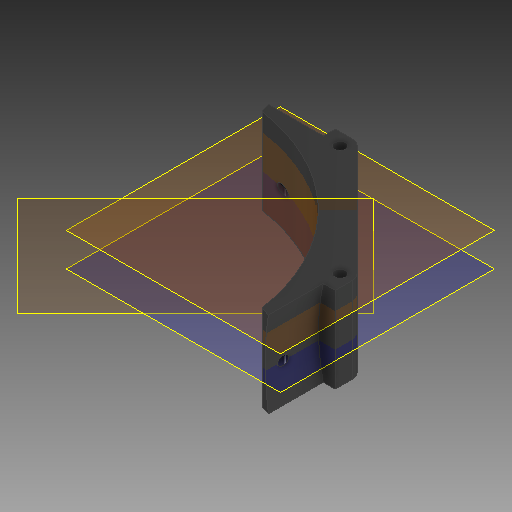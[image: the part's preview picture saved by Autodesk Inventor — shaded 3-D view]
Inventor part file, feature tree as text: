
AUTODESK INVENTOR PART (.ipt)
format: ipt  version: 2020 (Build 240168000, 168)  size: 210,944 bytes
history: native  units: mm
features: sketch x8, extrude x7, other x4, mirror x1, hole x1
ambient origin geometry x8: Origin, YZ Plane, XZ Plane, XY Plane, X Axis, Y Axis, Z Axis, Center Point
bodies: Body1 (feature_tree)
feature tree (21):
  other  "Твердое тело1"
  sketch  "Эскиз1"
  extrude  "Выдавливание1"  Depth=9.0mm
  other  "РабПлоскость1"
  extrude  "Выдавливание2"  Depth=9.0mm
  extrude  "Выдавливание3"  Depth=32.0mm TaperAngle=0.0deg
  other  "РабПлоскость2"
  mirror  "Зеркальное отражение1"
  extrude  "Выдавливание5"  [1 undecoded]
  other  "РабПлоскость4"
  extrude  "Выдавливание6"  Depth=20.6mm TaperAngle=0.0deg
  extrude  "Выдавливание7"  Depth=20.5mm TaperAngle=0.0deg
  hole  "Отверстие1"  [1 undecoded]
  extrude  "Выдавливание8"  Depth=7.485mm
  sketch  "Эскиз2"
  sketch  "Эскиз3"
  sketch  "Эскиз4"
  sketch  "Эскиз6"
  sketch  "Эскиз9"
  sketch  "Эскиз10"
  sketch  "Эскиз11"
note: 2 required parameter values undecoded (feature->parameter linkage not recoverable at this tier; creation-order binding heuristic only, values carry confidence <= 0.55)
